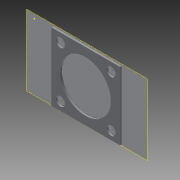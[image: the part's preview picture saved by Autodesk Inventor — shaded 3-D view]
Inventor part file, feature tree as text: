
AUTODESK INVENTOR PART (.ipt)
format: ipt  version: 2013 (Build 170138000, 138)  size: 371,712 bytes
history: native  units: in
note: dims shown in document units (in); Inventor stores cm internally (conversion verified against a paired STEP export)
features: sketch x2, other x2, extrude x1
ambient origin geometry x8: Origin, YZ Plane, XZ Plane, XY Plane, X Axis, Y Axis, Z Axis, Center Point
bodies: Solid1 (feature_tree)
feature tree (5):
  sketch  "Sketch1"  dims[d2=0.25in d3=0.0in]
  extrude  "Extrusion1"  [1 undecoded]
  other  "Image1"
  other  "Image2"
  sketch  "Sketch2"
note: 1 required parameter value undecoded (feature->parameter linkage not recoverable at this tier; creation-order binding heuristic only, values carry confidence <= 0.55)
